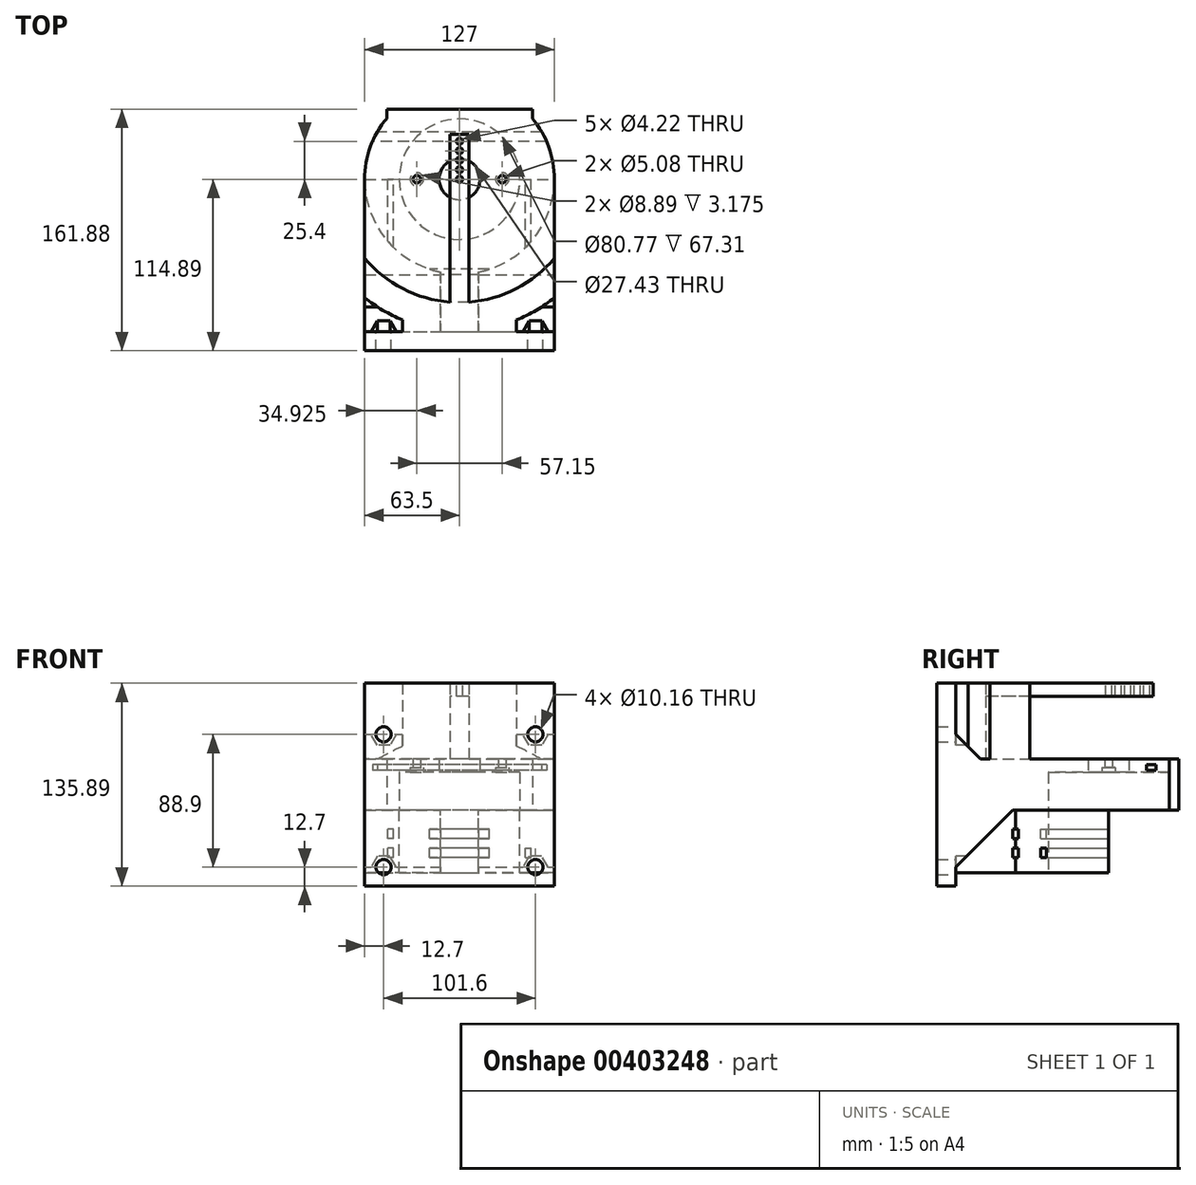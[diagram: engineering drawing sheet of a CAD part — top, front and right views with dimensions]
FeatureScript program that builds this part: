
annotation { "Feature Type Name" : "Feature", "Feature Type Description" : "" }
export const myFeature = defineFeature(function(context is Context, id is Id, definition is map)
    precondition{}
    {
        {
            var Q0;
            Q0=qCreatedBy(makeId("Top.planeOp"),FACE);
            var sketch = newSketch(context, id + "F0", { "sketchPlane" : qUnion([Q0])});
            skCircle(sketch, "E0", {"center": v(0, 0) * mm, "radius": 40.39 * mm});
            skArc(sketch, "E1", {"start": v(63.5, 0) * mm, "mid": v(0, 63.5) * mm, "end": v(-63.5, 0) * mm});
            skLineSegment(sketch, "E2.top", {"start": v(63.5, -102.19) * mm, "end": v(-63.5, -102.19) * mm});
            skLineSegment(sketch, "E2.left", {"start": v(63.5, 0) * mm, "end": v(63.5, -102.19) * mm});
            skLineSegment(sketch, "E2.right", {"start": v(-63.5, 0) * mm, "end": v(-63.5, -102.19) * mm});
            skSolve(sketch);
        }
        {
            var Q0;
            Q0 = qSketchRegion(id + "F0", true);
            extrude(context, id + "F1", {"entities" : qUnion([Q0]), "depth" : 25.4 * mm});
        }
        {
            var Q0;
            Q0=makeQuery(id+"F1.opExtrude","CAP_FACE",FACE,{"disambiguationData":[OSD([sQuery(id+"F0.wireOp",EDGE,"E0"),sQuery(id+"F0.wireOp",EDGE,"E1"),sQuery(id+"F0.wireOp",EDGE,"E2.top"),sQuery(id+"F0.wireOp",EDGE,"E2.left"),sQuery(id+"F0.wireOp",EDGE,"E2.right")])],"isStart":false});
            var sketch = newSketch(context, id + "F2", { "sketchPlane" : qUnion([Q0])});
            skCircle(sketch, "E3", {"center": v(0, 0) * mm, "radius": 63.5 * mm});
            skCircle(sketch, "E4", {"center": v(0, 0) * mm, "radius": 13.72 * mm});
            skLineSegment(sketch, "E5", {"start": v(0, 0) * mm, "end": v(28.58, 0) * mm});
            skLineSegment(sketch, "E6", {"start": v(0, 0) * mm, "end": v(-28.58, 0) * mm});
            skCircle(sketch, "E7", {"center": v(28.58, 0) * mm, "radius": 2.54 * mm});
            skCircle(sketch, "E8", {"center": v(-28.58, 0) * mm, "radius": 2.54 * mm});
            skCircle(sketch, "E9", {"center": v(0, 0) * mm, "radius": 40.4 * mm});
            skSolve(sketch);
        }
        {
            var Q0;
            Q0 = qSketchRegion(id + "F2", true);
            var Q1;
            Q1=makeQuery(id+"F2.imprint","IMPRINT",FACE,{"disambiguationData":[TD([[makeQuery(id+"F2.imprint","IMPRINT",EDGE,{"derivedFrom":sQuery(id+"F2.wireOp",EDGE,"E7")}),-1.0]])]});
            extrude(context, id + "F3", {"entities" : qUnion([Q0, Q1]), "operationType" : NewBodyOperationType.ADD, "depth" : 8.9 * mm});
        }
        {
            var Q0;
            Q0=makeQuery(id+"F1.opExtrude","SWEPT_FACE",FACE,{"disambiguationData":[OSD([sQuery(id+"F0.wireOp",EDGE,"E2.top")])]});
            var sketch = newSketch(context, id + "F4", { "sketchPlane" : qUnion([Q0])});
            skLineSegment(sketch, "E10.bottom", {"start": v(-63.5, 25.4) * mm, "end": v(63.5, 25.4) * mm});
            skLineSegment(sketch, "E10.top", {"start": v(-63.5, 0) * mm, "end": v(63.5, 0) * mm});
            skLineSegment(sketch, "E10.left", {"start": v(-63.5, 25.4) * mm, "end": v(-63.5, 0) * mm});
            skLineSegment(sketch, "E10.right", {"start": v(63.5, 25.4) * mm, "end": v(63.5, 0) * mm});
            skLineSegment(sketch, "E11.top", {"start": v(-63.5, 76.2) * mm, "end": v(63.5, 76.2) * mm});
            skLineSegment(sketch, "E11.left", {"start": v(-63.5, 25.4) * mm, "end": v(-63.5, 76.2) * mm});
            skLineSegment(sketch, "E11.right", {"start": v(63.5, 25.4) * mm, "end": v(63.5, 76.2) * mm});
            skLineSegment(sketch, "E12.top", {"start": v(-63.5, -50.8) * mm, "end": v(63.5, -50.8) * mm});
            skLineSegment(sketch, "E12.left", {"start": v(-63.5, 0) * mm, "end": v(-63.5, -50.8) * mm});
            skLineSegment(sketch, "E12.right", {"start": v(63.5, 0) * mm, "end": v(63.5, -50.8) * mm});
            skSolve(sketch);
        }
        {
            var Q0;
            Q0=makeQuery(id+"F4.imprint","IMPRINT",FACE,{"disambiguationData":[TD([[makeQuery(id+"F4.imprint","IMPRINT",EDGE,{"derivedFrom":sQuery(id+"F4.wireOp",EDGE,"E10.bottom")}),-1.0]])]});
            var Q1;
            Q1=makeQuery(id+"F4.imprint","IMPRINT",FACE,{"disambiguationData":[TD([[makeQuery(id+"F4.imprint","IMPRINT",EDGE,{"derivedFrom":sQuery(id+"F4.wireOp",EDGE,"E10.left")}),1.0]])]});
            var Q2;
            Q2=makeQuery(id+"F4.imprint","IMPRINT",FACE,{"disambiguationData":[TD([[makeQuery(id+"F4.imprint","IMPRINT",EDGE,{"derivedFrom":sQuery(id+"F4.wireOp",EDGE,"E10.top")}),1.0]])]});
            extrude(context, id + "F5", {"entities" : qUnion([Q0, Q1, Q2]), "operationType" : NewBodyOperationType.ADD, "depth" : 12.7 * mm});
        }
        {
            var Q0;
            Q0=makeQuery(id+"F5.boolean.opBoolean","MERGE",FACE,{"derivedFrom":[makeQuery(id+"F1.opExtrude","SWEPT_FACE",FACE,{"disambiguationData":[OSD([sQuery(id+"F0.wireOp",EDGE,"E2.left")])]}),makeQuery(id+"F5.opExtrude","SWEPT_FACE",FACE,{"disambiguationData":[OSD([sQuery(id+"F4.wireOp",EDGE,"E10.right"),sQuery(id+"F4.wireOp",EDGE,"E11.right"),sQuery(id+"F4.wireOp",EDGE,"E12.right")])]})]});
            var sketch = newSketch(context, id + "F6", { "sketchPlane" : qUnion([Q0])});
            skLineSegment(sketch, "E13.bottom", {"start": v(-102.19, 25.4) * mm, "end": v(-76.79, 25.4) * mm});
            skLineSegment(sketch, "E13.top", {"start": v(-102.19, 50.8) * mm, "end": v(-76.79, 50.8) * mm});
            skLineSegment(sketch, "E13.left", {"start": v(-102.19, 25.4) * mm, "end": v(-102.19, 50.8) * mm});
            skLineSegment(sketch, "E13.right", {"start": v(-76.79, 25.4) * mm, "end": v(-76.79, 50.8) * mm});
            skLineSegment(sketch, "E14.bottom", {"start": v(-102.19, 0) * mm, "end": v(-64.09, 0) * mm});
            skLineSegment(sketch, "E14.top", {"start": v(-102.19, -38.1) * mm, "end": v(-64.09, -38.1) * mm});
            skLineSegment(sketch, "E14.left", {"start": v(-102.19, 0) * mm, "end": v(-102.19, -38.1) * mm});
            skLineSegment(sketch, "E14.right", {"start": v(-64.09, 0) * mm, "end": v(-64.09, -38.1) * mm});
            skLineSegment(sketch, "E15", {"start": v(-102.19, -38.1) * mm, "end": v(-64.09, 0) * mm});
            skLineSegment(sketch, "E16", {"start": v(-76.79, 25.4) * mm, "end": v(-102.19, 50.8) * mm});
            skSolve(sketch);
        }
        {
            var Q0;
            Q0=makeQuery(id+"F6.imprint","IMPRINT",FACE,{"disambiguationData":[TD([[makeQuery(id+"F6.imprint","IMPRINT",EDGE,{"derivedFrom":sQuery(id+"F6.wireOp",EDGE,"E13.bottom")}),-1.0]])]});
            var Q1;
            Q1=makeQuery(id+"F6.imprint","IMPRINT",FACE,{"disambiguationData":[TD([[makeQuery(id+"F6.imprint","IMPRINT",EDGE,{"derivedFrom":sQuery(id+"F6.wireOp",EDGE,"E14.bottom")}),1.0]])]});
            extrude(context, id + "F7", {"entities" : qUnion([Q0, Q1]), "operationType" : NewBodyOperationType.ADD, "oppositeDirection" : true, "depth" : 127 * mm});
        }
        {
            var Q0;
            Q0=makeQuery(id+"F3.boolean.opBoolean","MERGE",FACE,{"derivedFrom":[makeQuery(id+"F3.opExtrude","CAP_FACE",FACE,{"disambiguationData":[OSD([sQuery(id+"F2.wireOp",EDGE,"E3"),sQuery(id+"F2.wireOp",EDGE,"E9")])],"isStart":false}),makeQuery(id+"F3.opExtrude","CAP_FACE",FACE,{"disambiguationData":[OSD([sQuery(id+"F0.wireOp",EDGE,"E0"),sQuery(id+"F2.wireOp",EDGE,"E4"),sQuery(id+"F2.wireOp",EDGE,"E7"),sQuery(id+"F2.wireOp",EDGE,"E8")])],"isStart":false})]});
            var sketch = newSketch(context, id + "F8", { "sketchPlane" : qUnion([Q0])});
            skCircle(sketch, "E17", {"center": v(0, 0) * mm, "radius": 101.6 * mm});
            skSolve(sketch);
        }
        {
            var Q0;
            Q0 = qSketchRegion(id + "F8", true);
            extrude(context, id + "F9", {"entities" : qUnion([Q0]), "operationType" : NewBodyOperationType.REMOVE, "depth" : 25.4 * mm});
        }
        {
            var Q0;
            {var subQ0=sQuery(id+"F4.wireOp",EDGE,"E12.left");var subQ1=sQuery(id+"F4.wireOp",EDGE,"E11.left");var subQ2=sQuery(id+"F4.wireOp",EDGE,"E10.left");var subQ5=sQuery(id+"F4.wireOp",EDGE,"E12.right");var subQ6=sQuery(id+"F4.wireOp",EDGE,"E11.right");var subQ7=sQuery(id+"F4.wireOp",EDGE,"E10.right");var subQ8=sQuery(id+"F4.wireOp",EDGE,"E12.top");Q0=makeQuery(id+"F5.boolean.opBoolean","SPLIT",FACE,{"disambiguationData":[TD([makeQuery(id+"F5.opExtrude","SWEPT_FACE",FACE,{"disambiguationData":[OSD([subQ8])]})])],"derivedFrom":makeQuery(id+"F5.opExtrude","CAP_FACE",FACE,{"disambiguationData":[OSD([subQ2,subQ7,sQuery(id+"F4.wireOp",EDGE,"E11.top"),subQ1,subQ6,subQ8,subQ0,subQ5])],"isStart":true})});}
            var sketch = newSketch(context, id + "F10", { "sketchPlane" : qUnion([Q0])});
            skLineSegment(sketch, "E18.bottom", {"start": v(-63.5, -50.8) * mm, "end": v(63.5, -50.8) * mm});
            skLineSegment(sketch, "E18.top", {"start": v(-63.5, 76.2) * mm, "end": v(63.5, 76.2) * mm});
            skLineSegment(sketch, "E18.left", {"start": v(-63.5, -50.8) * mm, "end": v(-63.5, 76.2) * mm});
            skLineSegment(sketch, "E18.right", {"start": v(63.5, -50.8) * mm, "end": v(63.5, 76.2) * mm});
            skLineSegment(sketch, "E19.bottom", {"start": v(-63.5, -50.8) * mm, "end": v(-38.1, -50.8) * mm});
            skLineSegment(sketch, "E19.top", {"start": v(-63.5, -25.4) * mm, "end": v(-38.1, -25.4) * mm});
            skLineSegment(sketch, "E19.left", {"start": v(-63.5, -50.8) * mm, "end": v(-63.5, -25.4) * mm});
            skLineSegment(sketch, "E19.right", {"start": v(-38.1, -50.8) * mm, "end": v(-38.1, -25.4) * mm});
            skLineSegment(sketch, "E20.bottom", {"start": v(63.5, -50.8) * mm, "end": v(38.1, -50.8) * mm});
            skLineSegment(sketch, "E20.top", {"start": v(63.5, -25.4) * mm, "end": v(38.1, -25.4) * mm});
            skLineSegment(sketch, "E20.left", {"start": v(63.5, -50.8) * mm, "end": v(63.5, -25.4) * mm});
            skLineSegment(sketch, "E20.right", {"start": v(38.1, -50.8) * mm, "end": v(38.1, -25.4) * mm});
            skLineSegment(sketch, "E21.bottom", {"start": v(-63.5, 76.2) * mm, "end": v(-50.8, 76.2) * mm});
            skLineSegment(sketch, "E21.top", {"start": v(-63.5, 50.8) * mm, "end": v(-50.8, 50.8) * mm});
            skLineSegment(sketch, "E21.left", {"start": v(-63.5, 76.2) * mm, "end": v(-63.5, 50.8) * mm});
            skLineSegment(sketch, "E21.right", {"start": v(-50.8, 76.2) * mm, "end": v(-50.8, 50.8) * mm});
            skLineSegment(sketch, "E22.bottom", {"start": v(63.5, 76.2) * mm, "end": v(50.8, 76.2) * mm});
            skLineSegment(sketch, "E22.top", {"start": v(63.5, 50.8) * mm, "end": v(50.8, 50.8) * mm});
            skLineSegment(sketch, "E22.left", {"start": v(63.5, 76.2) * mm, "end": v(63.5, 50.8) * mm});
            skLineSegment(sketch, "E22.right", {"start": v(50.8, 76.2) * mm, "end": v(50.8, 50.8) * mm});
            skCircle(sketch, "E23.cCircle", {"center": v(-50.8, 50.8) * mm, "radius": 7.3 * mm, "construction": true});
            skLineSegment(sketch, "E23.0", {"start": v(-46.57, 58.1) * mm, "end": v(-42.37, 50.79) * mm});
            skLineSegment(sketch, "E23.1", {"start": v(-42.37, 50.79) * mm, "end": v(-46.6, 43.5) * mm});
            skLineSegment(sketch, "E23.2", {"start": v(-46.6, 43.5) * mm, "end": v(-55.03, 43.5) * mm});
            skLineSegment(sketch, "E23.3", {"start": v(-55.03, 43.5) * mm, "end": v(-59.23, 50.81) * mm});
            skLineSegment(sketch, "E23.4", {"start": v(-59.23, 50.81) * mm, "end": v(-55, 58.1) * mm});
            skLineSegment(sketch, "E23.5", {"start": v(-55, 58.1) * mm, "end": v(-46.57, 58.1) * mm});
            skPoint(sketch, "E23.0.midPoint", {"position": v(-44.47, 54.44) * mm});
            skLineSegment(sketch, "E24.0.1.0", {"start": v(-46.6, -45.4) * mm, "end": v(-55.03, -45.4) * mm});
            skLineSegment(sketch, "E24.0.1.1", {"start": v(-55.03, -45.4) * mm, "end": v(-59.23, -38.09) * mm});
            skPoint(sketch, "E24.0.1.2", {"position": v(-44.47, -34.46) * mm});
            skLineSegment(sketch, "E24.0.1.3", {"start": v(-42.37, -38.11) * mm, "end": v(-46.6, -45.4) * mm});
            skLineSegment(sketch, "E24.0.1.4", {"start": v(-59.23, -38.09) * mm, "end": v(-55, -30.8) * mm});
            skCircle(sketch, "E24.0.1.5", {"center": v(-50.8, -38.1) * mm, "radius": 7.3 * mm, "construction": true});
            skLineSegment(sketch, "E24.0.1.6", {"start": v(-55, -30.8) * mm, "end": v(-46.57, -30.8) * mm});
            skLineSegment(sketch, "E24.0.1.7", {"start": v(-46.57, -30.8) * mm, "end": v(-42.37, -38.11) * mm});
            skLineSegment(sketch, "E24.1.0.0", {"start": v(55, 43.5) * mm, "end": v(46.57, 43.5) * mm});
            skLineSegment(sketch, "E24.1.0.1", {"start": v(46.57, 43.5) * mm, "end": v(42.37, 50.81) * mm});
            skPoint(sketch, "E24.1.0.2", {"position": v(57.13, 54.44) * mm});
            skLineSegment(sketch, "E24.1.0.3", {"start": v(59.23, 50.79) * mm, "end": v(55, 43.5) * mm});
            skLineSegment(sketch, "E24.1.0.4", {"start": v(42.37, 50.81) * mm, "end": v(46.6, 58.1) * mm});
            skCircle(sketch, "E24.1.0.5", {"center": v(50.8, 50.8) * mm, "radius": 7.3 * mm, "construction": true});
            skLineSegment(sketch, "E24.1.0.6", {"start": v(46.6, 58.1) * mm, "end": v(55.03, 58.1) * mm});
            skLineSegment(sketch, "E24.1.0.7", {"start": v(55.03, 58.1) * mm, "end": v(59.23, 50.79) * mm});
            skLineSegment(sketch, "E24.1.1.0", {"start": v(55, -45.4) * mm, "end": v(46.57, -45.4) * mm});
            skLineSegment(sketch, "E24.1.1.1", {"start": v(46.57, -45.4) * mm, "end": v(42.37, -38.09) * mm});
            skPoint(sketch, "E24.1.1.2", {"position": v(57.13, -34.46) * mm});
            skLineSegment(sketch, "E24.1.1.3", {"start": v(59.23, -38.11) * mm, "end": v(55, -45.4) * mm});
            skLineSegment(sketch, "E24.1.1.4", {"start": v(42.37, -38.09) * mm, "end": v(46.6, -30.8) * mm});
            skCircle(sketch, "E24.1.1.5", {"center": v(50.8, -38.1) * mm, "radius": 7.3 * mm, "construction": true});
            skLineSegment(sketch, "E24.1.1.6", {"start": v(46.6, -30.8) * mm, "end": v(55.03, -30.8) * mm});
            skLineSegment(sketch, "E24.1.1.7", {"start": v(55.03, -30.8) * mm, "end": v(59.23, -38.11) * mm});
            skLineSegment(sketch, "E24.direction1", {"start": v(-55.03, 43.5) * mm, "end": v(46.57, 43.5) * mm, "construction": true});
            skLineSegment(sketch, "E24.direction2", {"start": v(-55.03, 43.5) * mm, "end": v(-55.03, -45.4) * mm, "construction": true});
            skSolve(sketch);
        }
        {
            var Q0;
            {var subQ7=sQuery(id+"F10.wireOp",EDGE,"E23.0");Q0=makeQuery(id+"F10.imprint","IMPRINT",FACE,{"disambiguationData":[TD([[makeQuery(id+"F10.imprint","IMPRINT",EDGE,{"derivedFrom":subQ7}),-1.0]])]});}
            var Q1;
            {var subQ0=sQuery(id+"F10.wireOp",EDGE,"E23.4");Q1=makeQuery(id+"F10.imprint","IMPRINT",FACE,{"disambiguationData":[TD([[makeQuery(id+"F10.imprint","IMPRINT",EDGE,{"derivedFrom":subQ0}),-1.0]])]});}
            var Q2;
            Q2=makeQuery(id+"F10.imprint","IMPRINT",FACE,{"disambiguationData":[TD([[makeQuery(id+"F10.imprint","IMPRINT",EDGE,{"derivedFrom":sQuery(id+"F10.wireOp",EDGE,"E24.1.0.0")}),-1.0]])]});
            var Q3;
            {var subQ0=sQuery(id+"F10.wireOp",EDGE,"E22.right");var subQ1=sQuery(id+"F10.wireOp",EDGE,"E22.top");var subQ2=makeQuery(id+"F10.imprint","INTERSECT",VERTEX,{"derivedFrom":[subQ1,subQ0]});Q3=makeQuery(id+"F10.imprint","IMPRINT",FACE,{"disambiguationData":[TD([[makeQuery(id+"F10.imprint","IMPRINT",EDGE,{"disambiguationData":[TD([[subQ2,1.0]])],"derivedFrom":subQ1}),-1.0]])]});}
            var Q4;
            {var subQ6=sQuery(id+"F10.wireOp",EDGE,"E24.1.1.0");Q4=makeQuery(id+"F10.imprint","IMPRINT",FACE,{"disambiguationData":[TD([[makeQuery(id+"F10.imprint","IMPRINT",EDGE,{"derivedFrom":subQ6}),-1.0]])]});}
            var Q5;
            {var subQ4=sQuery(id+"F10.wireOp",EDGE,"E24.1.1.4");Q5=makeQuery(id+"F10.imprint","IMPRINT",FACE,{"disambiguationData":[TD([[makeQuery(id+"F10.imprint","IMPRINT",EDGE,{"derivedFrom":subQ4}),-1.0]])]});}
            var Q6;
            {var subQ4=sQuery(id+"F10.wireOp",EDGE,"E24.0.1.4");Q6=makeQuery(id+"F10.imprint","IMPRINT",FACE,{"disambiguationData":[TD([[makeQuery(id+"F10.imprint","IMPRINT",EDGE,{"derivedFrom":subQ4}),-1.0]])]});}
            var Q7;
            {var subQ6=sQuery(id+"F10.wireOp",EDGE,"E24.0.1.0");Q7=makeQuery(id+"F10.imprint","IMPRINT",FACE,{"disambiguationData":[TD([[makeQuery(id+"F10.imprint","IMPRINT",EDGE,{"derivedFrom":subQ6}),-1.0]])]});}
            extrude(context, id + "F11", {"entities" : qUnion([Q0, Q1, Q2, Q3, Q4, Q5, Q6, Q7]), "operationType" : NewBodyOperationType.REMOVE, "depth" : 25.4 * mm});
        }
        {
            var Q0;
            {var subQ0=sQuery(id+"F4.wireOp",EDGE,"E12.left");var subQ1=sQuery(id+"F4.wireOp",EDGE,"E11.left");var subQ2=sQuery(id+"F4.wireOp",EDGE,"E10.left");var subQ5=sQuery(id+"F4.wireOp",EDGE,"E12.right");var subQ6=sQuery(id+"F4.wireOp",EDGE,"E11.right");var subQ7=sQuery(id+"F4.wireOp",EDGE,"E10.right");var subQ8=sQuery(id+"F4.wireOp",EDGE,"E11.top");Q0=makeQuery(id+"F11.boolean.opBoolean","MERGE",FACE,{"derivedFrom":[makeQuery(id+"F5.boolean.opBoolean","SPLIT",FACE,{"disambiguationData":[TD([makeQuery(id+"F5.opExtrude","SWEPT_FACE",FACE,{"disambiguationData":[OSD([subQ8])]})])],"derivedFrom":makeQuery(id+"F5.opExtrude","CAP_FACE",FACE,{"disambiguationData":[OSD([subQ2,subQ7,subQ8,subQ1,subQ6,sQuery(id+"F4.wireOp",EDGE,"E12.top"),subQ0,subQ5])],"isStart":true})}),makeQuery(id+"F11.opExtrude","CAP_FACE",FACE,{"disambiguationData":[OSD([sQuery(id+"F10.wireOp",EDGE,"E23.0"),sQuery(id+"F10.wireOp",EDGE,"E23.1"),sQuery(id+"F10.wireOp",EDGE,"E23.2"),sQuery(id+"F10.wireOp",EDGE,"E23.3"),sQuery(id+"F10.wireOp",EDGE,"E23.4"),sQuery(id+"F10.wireOp",EDGE,"E23.5")])],"isStart":true}),makeQuery(id+"F11.opExtrude","CAP_FACE",FACE,{"disambiguationData":[OSD([sQuery(id+"F10.wireOp",EDGE,"E24.1.0.0"),sQuery(id+"F10.wireOp",EDGE,"E24.1.0.1"),sQuery(id+"F10.wireOp",EDGE,"E24.1.0.3"),sQuery(id+"F10.wireOp",EDGE,"E24.1.0.4"),sQuery(id+"F10.wireOp",EDGE,"E24.1.0.6"),sQuery(id+"F10.wireOp",EDGE,"E24.1.0.7")])],"isStart":true})]});}
            var sketch = newSketch(context, id + "F12", { "sketchPlane" : qUnion([Q0])});
            skLineSegment(sketch, "E25.bottom", {"start": v(-63.5, 76.2) * mm, "end": v(63.5, 76.2) * mm});
            skLineSegment(sketch, "E25.top", {"start": v(-63.5, -50.8) * mm, "end": v(63.5, -50.8) * mm});
            skLineSegment(sketch, "E25.left", {"start": v(-63.5, 76.2) * mm, "end": v(-63.5, -50.8) * mm});
            skLineSegment(sketch, "E25.right", {"start": v(63.5, 76.2) * mm, "end": v(63.5, -50.8) * mm});
            skLineSegment(sketch, "E26.bottom", {"start": v(-63.5, 76.2) * mm, "end": v(-50.8, 76.2) * mm});
            skLineSegment(sketch, "E26.top", {"start": v(-63.5, 50.8) * mm, "end": v(-50.8, 50.8) * mm});
            skLineSegment(sketch, "E26.left", {"start": v(-63.5, 76.2) * mm, "end": v(-63.5, 50.8) * mm});
            skLineSegment(sketch, "E26.right", {"start": v(-50.8, 76.2) * mm, "end": v(-50.8, 50.8) * mm});
            skLineSegment(sketch, "E27.bottom", {"start": v(63.5, 76.2) * mm, "end": v(50.8, 76.2) * mm});
            skLineSegment(sketch, "E27.top", {"start": v(63.5, 50.8) * mm, "end": v(50.8, 50.8) * mm});
            skLineSegment(sketch, "E27.left", {"start": v(63.5, 76.2) * mm, "end": v(63.5, 50.8) * mm});
            skLineSegment(sketch, "E27.right", {"start": v(50.8, 76.2) * mm, "end": v(50.8, 50.8) * mm});
            skLineSegment(sketch, "E28.bottom", {"start": v(-63.5, -50.8) * mm, "end": v(-50.8, -50.8) * mm});
            skLineSegment(sketch, "E28.top", {"start": v(-63.5, -38.1) * mm, "end": v(-50.8, -38.1) * mm});
            skLineSegment(sketch, "E28.left", {"start": v(-63.5, -50.8) * mm, "end": v(-63.5, -38.1) * mm});
            skLineSegment(sketch, "E28.right", {"start": v(-50.8, -50.8) * mm, "end": v(-50.8, -38.1) * mm});
            skLineSegment(sketch, "E29.bottom", {"start": v(63.5, -50.8) * mm, "end": v(50.8, -50.8) * mm});
            skLineSegment(sketch, "E29.top", {"start": v(63.5, -38.1) * mm, "end": v(50.8, -38.1) * mm});
            skLineSegment(sketch, "E29.left", {"start": v(63.5, -50.8) * mm, "end": v(63.5, -38.1) * mm});
            skLineSegment(sketch, "E29.right", {"start": v(50.8, -50.8) * mm, "end": v(50.8, -38.1) * mm});
            skCircle(sketch, "E30", {"center": v(-50.8, -38.1) * mm, "radius": 5.08 * mm});
            skCircle(sketch, "E31", {"center": v(50.8, -38.1) * mm, "radius": 5.08 * mm});
            skCircle(sketch, "E32", {"center": v(50.8, 50.8) * mm, "radius": 5.08 * mm});
            skCircle(sketch, "E33", {"center": v(-50.8, 50.8) * mm, "radius": 5.08 * mm});
            skSolve(sketch);
        }
        {
            var Q0;
            {var subQ0=sQuery(id+"F12.wireOp",EDGE,"E26.right");var subQ1=sQuery(id+"F12.wireOp",EDGE,"E26.top");var subQ2=makeQuery(id+"F12.imprint","INTERSECT",VERTEX,{"derivedFrom":[subQ1,subQ0]});Q0=makeQuery(id+"F12.imprint","IMPRINT",FACE,{"disambiguationData":[TD([[makeQuery(id+"F12.imprint","IMPRINT",EDGE,{"disambiguationData":[TD([[subQ2,1.0]])],"derivedFrom":subQ1}),1.0]])]});}
            var Q1;
            {var subQ0=sQuery(id+"F12.wireOp",EDGE,"E26.right");var subQ1=sQuery(id+"F12.wireOp",EDGE,"E26.top");var subQ2=makeQuery(id+"F12.imprint","INTERSECT",VERTEX,{"derivedFrom":[subQ1,subQ0]});Q1=makeQuery(id+"F12.imprint","IMPRINT",FACE,{"disambiguationData":[TD([[makeQuery(id+"F12.imprint","IMPRINT",EDGE,{"disambiguationData":[TD([[subQ2,1.0]])],"derivedFrom":subQ1}),-1.0]])]});}
            var Q2;
            {var subQ0=sQuery(id+"F12.wireOp",EDGE,"E27.right");var subQ1=sQuery(id+"F12.wireOp",EDGE,"E27.top");var subQ2=makeQuery(id+"F12.imprint","INTERSECT",VERTEX,{"derivedFrom":[subQ1,subQ0]});Q2=makeQuery(id+"F12.imprint","IMPRINT",FACE,{"disambiguationData":[TD([[makeQuery(id+"F12.imprint","IMPRINT",EDGE,{"disambiguationData":[TD([[subQ2,1.0]])],"derivedFrom":subQ1}),-1.0]])]});}
            var Q3;
            {var subQ0=sQuery(id+"F12.wireOp",EDGE,"E27.right");var subQ1=sQuery(id+"F12.wireOp",EDGE,"E27.top");var subQ2=makeQuery(id+"F12.imprint","INTERSECT",VERTEX,{"derivedFrom":[subQ1,subQ0]});Q3=makeQuery(id+"F12.imprint","IMPRINT",FACE,{"disambiguationData":[TD([[makeQuery(id+"F12.imprint","IMPRINT",EDGE,{"disambiguationData":[TD([[subQ2,1.0]])],"derivedFrom":subQ1}),1.0]])]});}
            var Q4;
            {var subQ0=sQuery(id+"F12.wireOp",EDGE,"E29.right");var subQ1=sQuery(id+"F12.wireOp",EDGE,"E29.top");var subQ2=makeQuery(id+"F12.imprint","INTERSECT",VERTEX,{"derivedFrom":[subQ1,subQ0]});Q4=makeQuery(id+"F12.imprint","IMPRINT",FACE,{"disambiguationData":[TD([[makeQuery(id+"F12.imprint","IMPRINT",EDGE,{"disambiguationData":[TD([[subQ2,1.0]])],"derivedFrom":subQ1}),1.0]])]});}
            var Q5;
            {var subQ0=sQuery(id+"F12.wireOp",EDGE,"E29.right");var subQ1=sQuery(id+"F12.wireOp",EDGE,"E29.top");var subQ2=makeQuery(id+"F12.imprint","INTERSECT",VERTEX,{"derivedFrom":[subQ1,subQ0]});Q5=makeQuery(id+"F12.imprint","IMPRINT",FACE,{"disambiguationData":[TD([[makeQuery(id+"F12.imprint","IMPRINT",EDGE,{"disambiguationData":[TD([[subQ2,1.0]])],"derivedFrom":subQ1}),-1.0]])]});}
            var Q6;
            {var subQ0=sQuery(id+"F12.wireOp",EDGE,"E28.right");var subQ1=sQuery(id+"F12.wireOp",EDGE,"E28.top");var subQ2=makeQuery(id+"F12.imprint","INTERSECT",VERTEX,{"derivedFrom":[subQ1,subQ0]});Q6=makeQuery(id+"F12.imprint","IMPRINT",FACE,{"disambiguationData":[TD([[makeQuery(id+"F12.imprint","IMPRINT",EDGE,{"disambiguationData":[TD([[subQ2,1.0]])],"derivedFrom":subQ1}),1.0]])]});}
            var Q7;
            {var subQ0=sQuery(id+"F12.wireOp",EDGE,"E28.right");var subQ1=sQuery(id+"F12.wireOp",EDGE,"E28.top");var subQ2=makeQuery(id+"F12.imprint","INTERSECT",VERTEX,{"derivedFrom":[subQ1,subQ0]});Q7=makeQuery(id+"F12.imprint","IMPRINT",FACE,{"disambiguationData":[TD([[makeQuery(id+"F12.imprint","IMPRINT",EDGE,{"disambiguationData":[TD([[subQ2,1.0]])],"derivedFrom":subQ1}),-1.0]])]});}
            extrude(context, id + "F13", {"entities" : qUnion([Q0, Q1, Q2, Q3, Q4, Q5, Q6, Q7]), "operationType" : NewBodyOperationType.REMOVE, "oppositeDirection" : true, "depth" : 25.4 * mm});
        }
        {
            var Q0;
            Q0=makeQuery(id+"F1.opExtrude","CAP_FACE",FACE,{"disambiguationData":[OSD([sQuery(id+"F0.wireOp",EDGE,"E0"),sQuery(id+"F0.wireOp",EDGE,"E1"),sQuery(id+"F0.wireOp",EDGE,"E2.top"),sQuery(id+"F0.wireOp",EDGE,"E2.left"),sQuery(id+"F0.wireOp",EDGE,"E2.right")])],"isStart":false});
            var sketch = newSketch(context, id + "F14", { "sketchPlane" : qUnion([Q0])});
            skLineSegment(sketch, "E34.bottom", {"start": v(63.5, 0) * mm, "end": v(44.72, 0) * mm});
            skLineSegment(sketch, "E34.top", {"start": v(63.5, -88.9) * mm, "end": v(-63.5, -88.9) * mm});
            skLineSegment(sketch, "E34.left", {"start": v(63.5, 0) * mm, "end": v(63.5, -88.9) * mm});
            skLineSegment(sketch, "E34.right", {"start": v(-63.5, 0) * mm, "end": v(-63.5, -88.9) * mm});
            skLineSegment(sketch, "E35.top", {"start": v(44.72, -22.33) * mm, "end": v(-44.71, -22.33) * mm});
            skLineSegment(sketch, "E35.left", {"start": v(44.72, 0) * mm, "end": v(44.72, -22.33) * mm});
            skLineSegment(sketch, "E35.right", {"start": v(-44.71, 0) * mm, "end": v(-44.71, -22.33) * mm});
            skLineSegment(sketch, "E36.trimOffspring", {"start": v(-44.71, 0) * mm, "end": v(-63.5, 0) * mm});
            skSolve(sketch);
        }
        {
            var Q0;
            Q0 = qSketchRegion(id + "F14", true);
            extrude(context, id + "F15", {"entities" : qUnion([Q0]), "operationType" : NewBodyOperationType.ADD, "depth" : 8.9 * mm});
        }
        {
            var Q0;
            Q0=makeQuery(id+"F3.boolean.opBoolean","MERGE",FACE,{"derivedFrom":[makeQuery(id+"F3.opExtrude","CAP_FACE",FACE,{"disambiguationData":[OSD([sQuery(id+"F2.wireOp",EDGE,"E3"),sQuery(id+"F2.wireOp",EDGE,"E9")])],"isStart":true}),makeQuery(id+"F3.opExtrude","CAP_FACE",FACE,{"disambiguationData":[OSD([sQuery(id+"F0.wireOp",EDGE,"E0"),sQuery(id+"F2.wireOp",EDGE,"E4"),sQuery(id+"F2.wireOp",EDGE,"E7"),sQuery(id+"F2.wireOp",EDGE,"E8")])],"isStart":true})]});
            var sketch = newSketch(context, id + "F16", { "sketchPlane" : qUnion([Q0])});
            skCircle(sketch, "E37", {"center": v(-28.58, 0) * mm, "radius": 4.45 * mm});
            skCircle(sketch, "E38", {"center": v(28.58, 0) * mm, "radius": 4.45 * mm});
            skSolve(sketch);
        }
        {
            var Q0;
            Q0 = qSketchRegion(id + "F16", true);
            extrude(context, id + "F17", {"entities" : qUnion([Q0]), "operationType" : NewBodyOperationType.REMOVE, "oppositeDirection" : true, "depth" : 3.17 * mm});
        }
        {
            var Q0;
            Q0=makeQuery(id+"F15.boolean.opBoolean","MERGE",FACE,{"derivedFrom":[makeQuery(id+"F3.boolean.opBoolean","MERGE",FACE,{"derivedFrom":[makeQuery(id+"F3.opExtrude","CAP_FACE",FACE,{"disambiguationData":[OSD([sQuery(id+"F2.wireOp",EDGE,"E3"),sQuery(id+"F2.wireOp",EDGE,"E9")])],"isStart":false}),makeQuery(id+"F3.opExtrude","CAP_FACE",FACE,{"disambiguationData":[OSD([sQuery(id+"F0.wireOp",EDGE,"E0"),sQuery(id+"F2.wireOp",EDGE,"E4"),sQuery(id+"F2.wireOp",EDGE,"E7"),sQuery(id+"F2.wireOp",EDGE,"E8")])],"isStart":false})]}),makeQuery(id+"F9.boolean.opBoolean","COPY",FACE,{"derivedFrom":makeQuery(id+"F9.opExtrude","CAP_FACE",FACE,{"disambiguationData":[OSD([sQuery(id+"F8.wireOp",EDGE,"E17")])],"isStart":true})}),makeQuery(id+"F15.opExtrude","CAP_FACE",FACE,{"disambiguationData":[OSD([sQuery(id+"F14.wireOp",EDGE,"E34.bottom"),sQuery(id+"F14.wireOp",EDGE,"E34.top"),sQuery(id+"F14.wireOp",EDGE,"E34.left"),sQuery(id+"F14.wireOp",EDGE,"E34.right"),sQuery(id+"F14.wireOp",EDGE,"E35.top"),sQuery(id+"F14.wireOp",EDGE,"E35.left"),sQuery(id+"F14.wireOp",EDGE,"E35.right"),sQuery(id+"F14.wireOp",EDGE,"E36.trimOffspring")])],"isStart":false})]});
            var sketch = newSketch(context, id + "F18", { "sketchPlane" : qUnion([Q0])});
            skArc(sketch, "E39", {"start": v(-63.5, -79.31) * mm, "mid": v(0, -101.6) * mm, "end": v(63.5, -79.31) * mm});
            skArc(sketch, "E40", {"start": v(-63.5, -71) * mm, "mid": v(0, -95.25) * mm, "end": v(63.5, -71) * mm});
            skLineSegment(sketch, "E41", {"start": v(63.5, -79.31) * mm, "end": v(63.5, -71) * mm});
            skLineSegment(sketch, "E42", {"start": v(-63.5, -79.31) * mm, "end": v(-63.5, -71) * mm});
            skSolve(sketch);
        }
        {
            var Q0;
            Q0 = qSketchRegion(id + "F18", true);
            extrude(context, id + "F19", {"entities" : qUnion([Q0]), "operationType" : NewBodyOperationType.ADD, "depth" : 50.8 * mm});
        }
        {
            var Q0;
            Q0=makeQuery(id+"F1.opExtrude","CAP_FACE",FACE,{"disambiguationData":[OSD([sQuery(id+"F0.wireOp",EDGE,"E0"),sQuery(id+"F0.wireOp",EDGE,"E1"),sQuery(id+"F0.wireOp",EDGE,"E2.top"),sQuery(id+"F0.wireOp",EDGE,"E2.left"),sQuery(id+"F0.wireOp",EDGE,"E2.right")])],"isStart":true});
            var sketch = newSketch(context, id + "F20", { "sketchPlane" : qUnion([Q0])});
            skCircle(sketch, "E43", {"center": v(0, 0) * mm, "radius": 40.39 * mm});
            skCircle(sketch, "E44", {"center": v(0, 0) * mm, "radius": 63.5 * mm});
            skLineSegment(sketch, "E45", {"start": v(0, 0) * mm, "end": v(12.7, 0) * mm});
            skLineSegment(sketch, "E46.bottom", {"start": v(12.7, 0) * mm, "end": v(-12.7, 0) * mm});
            skLineSegment(sketch, "E46.top", {"start": v(12.7, 114.3) * mm, "end": v(-12.7, 114.3) * mm});
            skLineSegment(sketch, "E46.left", {"start": v(12.7, 0) * mm, "end": v(12.7, 114.3) * mm});
            skLineSegment(sketch, "E46.right", {"start": v(-12.7, 0) * mm, "end": v(-12.7, 114.3) * mm});
            skLineSegment(sketch, "E47", {"start": v(-63.5, 0) * mm, "end": v(63.5, 0) * mm});
            skSolve(sketch);
        }
        {
            var Q0;
            {var subQ0=sQuery(id+"F20.wireOp",EDGE,"E47");var subQ1=sQuery(id+"F20.wireOp",EDGE,"E43");var subQ2=makeQuery(id+"F20.imprint","INTERSECT",VERTEX,{"disambiguationData":[OD(0.0)],"derivedFrom":[subQ1,subQ0]});Q0=makeQuery(id+"F20.imprint","IMPRINT",FACE,{"disambiguationData":[TD([[makeQuery(id+"F20.imprint","IMPRINT",EDGE,{"disambiguationData":[TD([[subQ2,-1.0]])],"derivedFrom":subQ1}),1.0]])]});}
            var Q1;
            {var subQ0=sQuery(id+"F20.wireOp",EDGE,"E46.right");var subQ1=sQuery(id+"F20.wireOp",EDGE,"E43");var subQ2=makeQuery(id+"F20.imprint","INTERSECT",VERTEX,{"derivedFrom":[subQ1,subQ0]});Q1=makeQuery(id+"F20.imprint","IMPRINT",FACE,{"disambiguationData":[TD([[makeQuery(id+"F20.imprint","IMPRINT",EDGE,{"disambiguationData":[TD([[subQ2,-1.0]])],"derivedFrom":subQ1}),1.0]])]});}
            var Q2;
            {var subQ0=sQuery(id+"F20.wireOp",EDGE,"E47");var subQ1=sQuery(id+"F20.wireOp",EDGE,"E43");var subQ2=makeQuery(id+"F20.imprint","INTERSECT",VERTEX,{"disambiguationData":[OD(1.0)],"derivedFrom":[subQ1,subQ0]});Q2=makeQuery(id+"F20.imprint","IMPRINT",FACE,{"disambiguationData":[TD([[makeQuery(id+"F20.imprint","IMPRINT",EDGE,{"disambiguationData":[TD([[subQ2,1.0]])],"derivedFrom":subQ1}),1.0]])]});}
            var Q3;
            {var subQ0=sQuery(id+"F20.wireOp",EDGE,"E46.top");Q3=makeQuery(id+"F20.imprint","IMPRINT",FACE,{"disambiguationData":[TD([[makeQuery(id+"F20.imprint","IMPRINT",EDGE,{"derivedFrom":subQ0}),1.0]])]});}
            var Q4;
            {var subQ0=sQuery(id+"F20.wireOp",EDGE,"E46.left");var subQ1=sQuery(id+"F20.wireOp",EDGE,"E44");var subQ2=makeQuery(id+"F20.imprint","INTERSECT",VERTEX,{"derivedFrom":[subQ1,subQ0]});var subQ3=sQuery(id+"F20.wireOp",EDGE,"E46.right");var subQ4=makeQuery(id+"F20.imprint","INTERSECT",VERTEX,{"derivedFrom":[subQ1,subQ3]});Q4=makeQuery(id+"F20.imprint","IMPRINT",FACE,{"disambiguationData":[TD([[makeQuery(id+"F20.imprint","IMPRINT",EDGE,{"disambiguationData":[TD([[subQ2,-1.0],[subQ4,1.0]])],"derivedFrom":subQ1}),-1.0]])]});}
            extrude(context, id + "F21", {"entities" : qUnion([Q0, Q1, Q2, Q3, Q4]), "operationType" : NewBodyOperationType.ADD, "depth" : 41.9 * mm});
        }
        {
            var Q0;
            Q0=makeQuery(id+"F21.opExtrude","SWEPT_FACE",FACE,{"disambiguationData":[OSD([sQuery(id+"F20.wireOp",EDGE,"E46.right")])]});
            var sketch = newSketch(context, id + "F22", { "sketchPlane" : qUnion([Q0])});
            skLineSegment(sketch, "E48", {"start": v(64.09, 0) * mm, "end": v(64.09, -12.7) * mm});
            skLineSegment(sketch, "E49.bottom", {"start": v(64.09, -12.7) * mm, "end": v(60.28, -12.7) * mm});
            skLineSegment(sketch, "E49.top", {"start": v(64.09, -19.05) * mm, "end": v(60.28, -19.05) * mm});
            skLineSegment(sketch, "E49.left", {"start": v(64.09, -12.7) * mm, "end": v(64.09, -19.05) * mm});
            skLineSegment(sketch, "E49.right", {"start": v(60.28, -12.7) * mm, "end": v(60.28, -19.05) * mm});
            skLineSegment(sketch, "E50", {"start": v(64.09, -19.05) * mm, "end": v(64.09, -25.4) * mm});
            skLineSegment(sketch, "E51.bottom", {"start": v(64.09, -25.4) * mm, "end": v(60.28, -25.4) * mm});
            skLineSegment(sketch, "E51.top", {"start": v(64.09, -31.75) * mm, "end": v(60.28, -31.75) * mm});
            skLineSegment(sketch, "E51.left", {"start": v(64.09, -25.4) * mm, "end": v(64.09, -31.75) * mm});
            skLineSegment(sketch, "E51.right", {"start": v(60.28, -25.4) * mm, "end": v(60.28, -31.75) * mm});
            skSolve(sketch);
        }
        {
            var Q0;
            Q0 = qSketchRegion(id + "F22", true);
            extrude(context, id + "F23", {"entities" : qUnion([Q0]), "operationType" : NewBodyOperationType.REMOVE, "endBound" : BoundingType.SYMMETRIC, "oppositeDirection" : true, "depth" : 76.2 * mm});
        }
        {
            var Q0;
            {var subQ0=sQuery(id+"F20.wireOp",EDGE,"E47");Q0=makeQuery(id+"F21.opExtrude","SWEPT_FACE",FACE,{"disambiguationData":[OSD([subQ0]),TDD([makeQuery(id+"F20.imprint","IMPRINT",EDGE,{"disambiguationData":[TD([[makeQuery(id+"F20.imprint","INTERSECT",VERTEX,{"disambiguationData":[OD(0.0)],"derivedFrom":[sQuery(id+"F20.wireOp",EDGE,"E43"),subQ0]}),1.0]])],"derivedFrom":subQ0})])]});}
            var sketch = newSketch(context, id + "F24", { "sketchPlane" : qUnion([Q0])});
            skLineSegment(sketch, "E52", {"start": v(40.39, 0) * mm, "end": v(40.39, -12.7) * mm});
            skLineSegment(sketch, "E53.bottom", {"start": v(40.39, -12.7) * mm, "end": v(44.2, -12.7) * mm});
            skLineSegment(sketch, "E53.top", {"start": v(40.39, -19.05) * mm, "end": v(44.2, -19.05) * mm});
            skLineSegment(sketch, "E53.left", {"start": v(40.39, -12.7) * mm, "end": v(40.39, -19.05) * mm});
            skLineSegment(sketch, "E53.right", {"start": v(44.2, -12.7) * mm, "end": v(44.2, -19.05) * mm});
            skLineSegment(sketch, "E54", {"start": v(40.39, -19.05) * mm, "end": v(40.39, -25.4) * mm});
            skLineSegment(sketch, "E55.bottom", {"start": v(40.39, -25.4) * mm, "end": v(44.2, -25.4) * mm});
            skLineSegment(sketch, "E55.top", {"start": v(40.39, -31.75) * mm, "end": v(44.2, -31.75) * mm});
            skLineSegment(sketch, "E55.left", {"start": v(40.39, -25.4) * mm, "end": v(40.39, -31.75) * mm});
            skLineSegment(sketch, "E55.right", {"start": v(44.2, -25.4) * mm, "end": v(44.2, -31.75) * mm});
            skLineSegment(sketch, "E56.bottom", {"start": v(44.2, -31.75) * mm, "end": v(48, -31.75) * mm});
            skLineSegment(sketch, "E56.top", {"start": v(44.2, -25.4) * mm, "end": v(48, -25.4) * mm});
            skLineSegment(sketch, "E56.left", {"start": v(44.2, -31.75) * mm, "end": v(44.2, -25.4) * mm});
            skLineSegment(sketch, "E56.right", {"start": v(48, -31.75) * mm, "end": v(48, -25.4) * mm});
            skPoint(sketch, "E57.oppositeSnap0", {"position": v(48, -28.57) * mm});
            skLineSegment(sketch, "E57.bottom", {"start": v(44.2, -19.05) * mm, "end": v(48, -19.05) * mm});
            skLineSegment(sketch, "E57.top", {"start": v(44.2, -12.7) * mm, "end": v(48, -12.7) * mm});
            skLineSegment(sketch, "E57.left", {"start": v(44.2, -19.05) * mm, "end": v(44.2, -12.7) * mm});
            skLineSegment(sketch, "E57.right", {"start": v(48, -19.05) * mm, "end": v(48, -12.7) * mm});
            skLineSegment(sketch, "E58", {"start": v(0, 0) * mm, "end": v(0, -36.16) * mm});
            skLineSegment(sketch, "E59.MirrorCS", {"start": v(-44.2, -25.4) * mm, "end": v(-44.2, -31.75) * mm});
            skLineSegment(sketch, "E60.MirrorCS", {"start": v(-44.2, -19.05) * mm, "end": v(-44.2, -12.7) * mm});
            skLineSegment(sketch, "E61.MirrorCS", {"start": v(-44.2, -12.7) * mm, "end": v(-44.2, -19.05) * mm});
            skLineSegment(sketch, "E62.MirrorCS", {"start": v(-48, -19.05) * mm, "end": v(-48, -12.7) * mm});
            skLineSegment(sketch, "E63.MirrorCS", {"start": v(-44.2, -31.75) * mm, "end": v(-48, -31.75) * mm});
            skLineSegment(sketch, "E64.MirrorCS", {"start": v(-44.2, -12.7) * mm, "end": v(-48, -12.7) * mm});
            skLineSegment(sketch, "E65.MirrorCS", {"start": v(-44.2, -19.05) * mm, "end": v(-48, -19.05) * mm});
            skLineSegment(sketch, "E66.MirrorCS", {"start": v(-48, -31.75) * mm, "end": v(-48, -25.4) * mm});
            skLineSegment(sketch, "E67.MirrorCS", {"start": v(-44.2, -31.75) * mm, "end": v(-44.2, -25.4) * mm});
            skLineSegment(sketch, "E68.MirrorCS", {"start": v(-44.2, -25.4) * mm, "end": v(-48, -25.4) * mm});
            skPoint(sketch, "E69.MirrorP", {"position": v(-48, -28.57) * mm});
            skSolve(sketch);
        }
        {
            var Q0;
            Q0=makeQuery(id+"F24.imprint","IMPRINT",FACE,{"disambiguationData":[TD([[makeQuery(id+"F24.imprint","IMPRINT",EDGE,{"derivedFrom":sQuery(id+"F24.wireOp",EDGE,"E61.MirrorCS")}),-1.0]])]});
            var Q1;
            Q1=makeQuery(id+"F24.imprint","IMPRINT",FACE,{"disambiguationData":[TD([[makeQuery(id+"F24.imprint","IMPRINT",EDGE,{"derivedFrom":sQuery(id+"F24.wireOp",EDGE,"E63.MirrorCS")}),-1.0]])]});
            var Q2;
            Q2=makeQuery(id+"F24.imprint","IMPRINT",FACE,{"disambiguationData":[TD([[makeQuery(id+"F24.imprint","IMPRINT",EDGE,{"derivedFrom":sQuery(id+"F24.wireOp",EDGE,"E56.bottom")}),1.0]])]});
            var Q3;
            Q3=makeQuery(id+"F24.imprint","IMPRINT",FACE,{"disambiguationData":[TD([[makeQuery(id+"F24.imprint","IMPRINT",EDGE,{"derivedFrom":sQuery(id+"F24.wireOp",EDGE,"E57.bottom")}),1.0]])]});
            extrude(context, id + "F25", {"entities" : qUnion([Q0, Q1, Q2, Q3]), "operationType" : NewBodyOperationType.REMOVE, "oppositeDirection" : true, "depth" : 50.8 * mm});
        }
        {
            var Q0;
            Q0=makeQuery(id+"F19.boolean.opBoolean","MERGE",FACE,{"derivedFrom":[makeQuery(id+"F15.boolean.opBoolean","MERGE",FACE,{"derivedFrom":[makeQuery(id+"F7.boolean.opBoolean","MERGE",FACE,{"derivedFrom":[makeQuery(id+"F5.boolean.opBoolean","MERGE",FACE,{"derivedFrom":[makeQuery(id+"F1.opExtrude","SWEPT_FACE",FACE,{"disambiguationData":[OSD([sQuery(id+"F0.wireOp",EDGE,"E2.right")])]}),makeQuery(id+"F5.opExtrude","SWEPT_FACE",FACE,{"disambiguationData":[OSD([sQuery(id+"F4.wireOp",EDGE,"E10.left"),sQuery(id+"F4.wireOp",EDGE,"E11.left"),sQuery(id+"F4.wireOp",EDGE,"E12.left")])]})]}),makeQuery(id+"F7.opExtrude","CAP_FACE",FACE,{"disambiguationData":[OSD([sQuery(id+"F6.wireOp",EDGE,"E13.bottom"),sQuery(id+"F6.wireOp",EDGE,"E13.left"),sQuery(id+"F6.wireOp",EDGE,"E16")])],"isStart":false}),makeQuery(id+"F7.opExtrude","CAP_FACE",FACE,{"disambiguationData":[OSD([sQuery(id+"F6.wireOp",EDGE,"E14.bottom"),sQuery(id+"F6.wireOp",EDGE,"E14.left"),sQuery(id+"F6.wireOp",EDGE,"E15")])],"isStart":false})]}),makeQuery(id+"F15.opExtrude","SWEPT_FACE",FACE,{"disambiguationData":[OSD([sQuery(id+"F14.wireOp",EDGE,"E34.right")])]})]}),makeQuery(id+"F19.opExtrude","SWEPT_FACE",FACE,{"disambiguationData":[OSD([sQuery(id+"F18.wireOp",EDGE,"E42")])]})]});
            var sketch = newSketch(context, id + "F26", { "sketchPlane" : qUnion([Q0])});
            skLineSegment(sketch, "E70.bottom", {"start": v(0, 34.3) * mm, "end": v(-25.4, 34.3) * mm});
            skLineSegment(sketch, "E70.top", {"start": v(0, 30.48) * mm, "end": v(-25.4, 30.48) * mm});
            skLineSegment(sketch, "E70.left", {"start": v(0, 34.3) * mm, "end": v(0, 30.48) * mm});
            skLineSegment(sketch, "E70.right", {"start": v(-25.4, 34.3) * mm, "end": v(-25.4, 30.48) * mm});
            skLineSegment(sketch, "E71.bottom", {"start": v(-25.4, 30.48) * mm, "end": v(-31.75, 30.48) * mm});
            skLineSegment(sketch, "E71.top", {"start": v(-25.4, 26.67) * mm, "end": v(-31.75, 26.67) * mm});
            skLineSegment(sketch, "E71.left", {"start": v(-25.4, 30.48) * mm, "end": v(-25.4, 26.67) * mm});
            skLineSegment(sketch, "E71.right", {"start": v(-31.75, 30.48) * mm, "end": v(-31.75, 26.67) * mm});
            skSolve(sketch);
        }
        {
            var Q0;
            Q0=makeQuery(id+"F26.imprint","IMPRINT",FACE,{"disambiguationData":[TD([[makeQuery(id+"F26.imprint","IMPRINT",EDGE,{"derivedFrom":sQuery(id+"F26.wireOp",EDGE,"E71.bottom")}),1.0]])]});
            extrude(context, id + "F27", {"entities" : qUnion([Q0]), "operationType" : NewBodyOperationType.REMOVE, "endBound" : BoundingType.THROUGH_ALL, "oppositeDirection" : true, "depth" : 25.4 * mm});
        }
        {
            var Q0;
            {var subQ0=sQuery(id+"F20.wireOp",EDGE,"E47");Q0=makeQuery(id+"F21.opExtrude","SWEPT_FACE",FACE,{"disambiguationData":[OSD([subQ0]),TDD([makeQuery(id+"F20.imprint","IMPRINT",EDGE,{"disambiguationData":[TD([[makeQuery(id+"F20.imprint","INTERSECT",VERTEX,{"disambiguationData":[OD(1.0)],"derivedFrom":[sQuery(id+"F20.wireOp",EDGE,"E43"),subQ0]}),-1.0]])],"derivedFrom":subQ0})])]});}
            cPlane(context, id + "F28", {"entities" : qUnion([Q0]), "cplaneType" : CPlaneType.OFFSET, "offset" : 40.64 * mm, "width" : 152.4 * mm, "height" : 152.4 * mm});
        }
        {
            var Q0;
            Q0=qCreatedBy(id+"F28.planeOp",FACE);
            var sketch = newSketch(context, id + "F29", { "sketchPlane" : qUnion([Q0])});
            skLineSegment(sketch, "E72.bottom", {"start": v(112.57, 54.79) * mm, "end": v(-136.53, 54.79) * mm});
            skLineSegment(sketch, "E72.top", {"start": v(112.57, -28.85) * mm, "end": v(-136.53, -28.85) * mm});
            skLineSegment(sketch, "E72.left", {"start": v(112.57, 54.79) * mm, "end": v(112.57, -28.85) * mm});
            skLineSegment(sketch, "E72.right", {"start": v(-136.53, 54.79) * mm, "end": v(-136.53, -28.85) * mm});
            skSolve(sketch);
        }
        {
            var Q0;
            Q0=makeQuery(id+"F29.imprint","IMPRINT",FACE,{"disambiguationData":[TD([[makeQuery(id+"F29.imprint","IMPRINT",EDGE,{"derivedFrom":sQuery(id+"F29.wireOp",EDGE,"E72.bottom")}),1.0]])]});
            extrude(context, id + "F30", {"entities" : qUnion([Q0]), "operationType" : NewBodyOperationType.REMOVE, "depth" : 25.4 * mm});
        }
        {
            var Q0;
            {var subQ0=sQuery(id+"F4.wireOp",EDGE,"E12.left");var subQ1=sQuery(id+"F4.wireOp",EDGE,"E11.left");var subQ2=sQuery(id+"F4.wireOp",EDGE,"E10.left");var subQ5=sQuery(id+"F4.wireOp",EDGE,"E12.right");var subQ6=sQuery(id+"F4.wireOp",EDGE,"E11.right");var subQ7=sQuery(id+"F4.wireOp",EDGE,"E10.right");var subQ8=sQuery(id+"F4.wireOp",EDGE,"E11.top");Q0=makeQuery(id+"F11.boolean.opBoolean","MERGE",FACE,{"derivedFrom":[makeQuery(id+"F5.boolean.opBoolean","SPLIT",FACE,{"disambiguationData":[TD([makeQuery(id+"F5.opExtrude","SWEPT_FACE",FACE,{"disambiguationData":[OSD([subQ8])]})])],"derivedFrom":makeQuery(id+"F5.opExtrude","CAP_FACE",FACE,{"disambiguationData":[OSD([subQ2,subQ7,subQ8,subQ1,subQ6,sQuery(id+"F4.wireOp",EDGE,"E12.top"),subQ0,subQ5])],"isStart":true})}),makeQuery(id+"F11.opExtrude","CAP_FACE",FACE,{"disambiguationData":[OSD([sQuery(id+"F10.wireOp",EDGE,"E23.0"),sQuery(id+"F10.wireOp",EDGE,"E23.1"),sQuery(id+"F10.wireOp",EDGE,"E23.2"),sQuery(id+"F10.wireOp",EDGE,"E23.3"),sQuery(id+"F10.wireOp",EDGE,"E23.4"),sQuery(id+"F10.wireOp",EDGE,"E23.5")])],"isStart":true}),makeQuery(id+"F11.opExtrude","CAP_FACE",FACE,{"disambiguationData":[OSD([sQuery(id+"F10.wireOp",EDGE,"E24.1.0.0"),sQuery(id+"F10.wireOp",EDGE,"E24.1.0.1"),sQuery(id+"F10.wireOp",EDGE,"E24.1.0.3"),sQuery(id+"F10.wireOp",EDGE,"E24.1.0.4"),sQuery(id+"F10.wireOp",EDGE,"E24.1.0.6"),sQuery(id+"F10.wireOp",EDGE,"E24.1.0.7")])],"isStart":true})]});}
            cPlane(context, id + "F31", {"entities" : qUnion([Q0]), "cplaneType" : CPlaneType.OFFSET, "offset" : 5.08 * mm, "width" : 152.4 * mm, "height" : 152.4 * mm});
        }
        {
            var Q0;
            Q0=qCreatedBy(id+"F31.planeOp",FACE);
            var sketch = newSketch(context, id + "F32", { "sketchPlane" : qUnion([Q0])});
            skLineSegment(sketch, "E73", {"start": v(0, 0) * mm, "end": v(0, 82.55) * mm});
            skLineSegment(sketch, "E74.bottom", {"start": v(0, 82.55) * mm, "end": v(6.35, 82.55) * mm});
            skLineSegment(sketch, "E74.top", {"start": v(0, 76.2) * mm, "end": v(6.35, 76.2) * mm});
            skLineSegment(sketch, "E74.left", {"start": v(0, 82.55) * mm, "end": v(0, 76.2) * mm});
            skLineSegment(sketch, "E74.right", {"start": v(6.35, 82.55) * mm, "end": v(6.35, 76.2) * mm});
            skLineSegment(sketch, "E75.bottom", {"start": v(0, 82.55) * mm, "end": v(-6.35, 82.55) * mm});
            skLineSegment(sketch, "E75.top", {"start": v(0, 76.2) * mm, "end": v(-6.35, 76.2) * mm});
            skLineSegment(sketch, "E75.right", {"start": v(-6.35, 82.55) * mm, "end": v(-6.35, 76.2) * mm});
            skSolve(sketch);
        }
        {
            var Q0;
            Q0 = qSketchRegion(id + "F32", true);
            extrude(context, id + "F33", {"entities" : qUnion([Q0]), "operationType" : NewBodyOperationType.ADD, "depth" : 127 * mm});
        }
        {
            var Q0;
            Q0=makeQuery(id+"F33.opExtrude","SWEPT_FACE",FACE,{"disambiguationData":[OSD([sQuery(id+"F32.wireOp",EDGE,"E74.bottom"),sQuery(id+"F32.wireOp",EDGE,"E75.bottom")])]});
            var sketch = newSketch(context, id + "F34", { "sketchPlane" : qUnion([Q0])});
            skSolve(sketch);
        }
        {
            var Q0;
            Q0 = qSketchRegion(id + "F34", true);
            var Q1;
            {var subQ0=sQuery(id+"F32.wireOp",EDGE,"E75.bottom");var subQ1=sQuery(id+"F32.wireOp",EDGE,"E74.bottom");Q1=makeQuery(id+"F34.imprint","IMPRINT",FACE,{"disambiguationData":[TD([[makeQuery(id+"F34.imprint","IMPRINT",EDGE,{"derivedFrom":makeQuery(id+"F33.opExtrude","CAP_EDGE",EDGE,{"disambiguationData":[OSD([subQ1,subQ0])],"isStart":false})}),1.0]])]});}
            extrude(context, id + "F35", {"entities" : qUnion([Q0, Q1]), "operationType" : NewBodyOperationType.ADD, "depth" : 2.54 * mm});
        }
        {
            var Q0;
            {var subQ0=sQuery(id+"F18.wireOp",EDGE,"E40");Q0=makeQuery(id+"F35.boolean.opBoolean","MERGE",FACE,{"derivedFrom":[makeQuery(id+"F19.opExtrude","CAP_FACE",FACE,{"disambiguationData":[OSD([sQuery(id+"F18.wireOp",EDGE,"E39"),subQ0,sQuery(id+"F18.wireOp",EDGE,"E41"),sQuery(id+"F18.wireOp",EDGE,"E42")])],"isStart":false}),makeQuery(id+"F35.opExtrude","CAP_FACE",FACE,{"disambiguationData":[OSD([subQ0,sQuery(id+"F32.wireOp",EDGE,"E74.bottom"),sQuery(id+"F32.wireOp",EDGE,"E74.right"),sQuery(id+"F32.wireOp",EDGE,"E75.bottom"),sQuery(id+"F32.wireOp",EDGE,"E75.right")])],"isStart":false})]});}
            var sketch = newSketch(context, id + "F36", { "sketchPlane" : qUnion([Q0])});
            skCircle(sketch, "E76", {"center": v(0, 0) * mm, "radius": 2.1 * mm});
            skCircle(sketch, "E77.0.1.0", {"center": v(0, 6.35) * mm, "radius": 2.1 * mm});
            skCircle(sketch, "E77.0.2.0", {"center": v(0, 12.7) * mm, "radius": 2.1 * mm});
            skCircle(sketch, "E77.0.3.0", {"center": v(0, 19.05) * mm, "radius": 2.1 * mm});
            skCircle(sketch, "E77.0.4.0", {"center": v(0, 25.4) * mm, "radius": 2.1 * mm});
            skCircle(sketch, "E77.1.0.0", {"center": v(25.4, 0) * mm, "radius": 2.1 * mm});
            skCircle(sketch, "E77.1.1.0", {"center": v(25.4, 6.35) * mm, "radius": 2.1 * mm});
            skCircle(sketch, "E77.1.2.0", {"center": v(25.4, 12.7) * mm, "radius": 2.1 * mm});
            skCircle(sketch, "E77.1.3.0", {"center": v(25.4, 19.05) * mm, "radius": 2.1 * mm});
            skCircle(sketch, "E77.1.4.0", {"center": v(25.4, 25.4) * mm, "radius": 2.1 * mm});
            skCircle(sketch, "E77.2.0.0", {"center": v(50.8, 0) * mm, "radius": 2.1 * mm});
            skCircle(sketch, "E77.2.1.0", {"center": v(50.8, 6.35) * mm, "radius": 2.1 * mm});
            skCircle(sketch, "E77.2.2.0", {"center": v(50.8, 12.7) * mm, "radius": 2.1 * mm});
            skCircle(sketch, "E77.2.3.0", {"center": v(50.8, 19.05) * mm, "radius": 2.1 * mm});
            skCircle(sketch, "E77.2.4.0", {"center": v(50.8, 25.4) * mm, "radius": 2.1 * mm});
            skLineSegment(sketch, "E77.direction1", {"start": v(0, 0) * mm, "end": v(25.4, 0) * mm, "construction": true});
            skLineSegment(sketch, "E77.direction2", {"start": v(0, 0) * mm, "end": v(0, 6.35) * mm, "construction": true});
            skSolve(sketch);
        }
        {
            var Q0;
            Q0=makeQuery(id+"F36.imprint","IMPRINT",FACE,{"disambiguationData":[TD([[makeQuery(id+"F36.imprint","IMPRINT",EDGE,{"derivedFrom":sQuery(id+"F36.wireOp",EDGE,"E76")}),1.0]])]});
            var Q1;
            Q1=makeQuery(id+"F36.imprint","IMPRINT",FACE,{"disambiguationData":[TD([[makeQuery(id+"F36.imprint","IMPRINT",EDGE,{"derivedFrom":sQuery(id+"F36.wireOp",EDGE,"E77.0.1.0")}),1.0]])]});
            var Q2;
            Q2=makeQuery(id+"F36.imprint","IMPRINT",FACE,{"disambiguationData":[TD([[makeQuery(id+"F36.imprint","IMPRINT",EDGE,{"derivedFrom":sQuery(id+"F36.wireOp",EDGE,"E77.0.3.0")}),1.0]])]});
            var Q3;
            Q3=makeQuery(id+"F36.imprint","IMPRINT",FACE,{"disambiguationData":[TD([[makeQuery(id+"F36.imprint","IMPRINT",EDGE,{"derivedFrom":sQuery(id+"F36.wireOp",EDGE,"E77.0.4.0")}),1.0]])]});
            var Q4;
            Q4=makeQuery(id+"F36.imprint","IMPRINT",FACE,{"disambiguationData":[TD([[makeQuery(id+"F36.imprint","IMPRINT",EDGE,{"derivedFrom":sQuery(id+"F36.wireOp",EDGE,"E77.0.2.0")}),1.0]])]});
            extrude(context, id + "F37", {"entities" : qUnion([Q0, Q1, Q2, Q3, Q4]), "operationType" : NewBodyOperationType.REMOVE, "oppositeDirection" : true, "depth" : 25.4 * mm});
        }
        {
            var Q0;
            Q0=makeQuery(id+"F5.opExtrude","SWEPT_FACE",FACE,{"disambiguationData":[OSD([sQuery(id+"F4.wireOp",EDGE,"E11.top")])]});
            extrude(context, id + "F38", {"entities" : qUnion([Q0]), "operationType" : NewBodyOperationType.ADD, "depth" : 8.9 * mm});
        }
        {
            var Q0;
            {var subQ0=sQuery(id+"F2.wireOp",EDGE,"E8");var subQ1=sQuery(id+"F2.wireOp",EDGE,"E7");var subQ2=sQuery(id+"F2.wireOp",EDGE,"E4");var subQ3=sQuery(id+"F6.wireOp",EDGE,"E16");var subQ4=sQuery(id+"F6.wireOp",EDGE,"E13.left");var subQ5=sQuery(id+"F6.wireOp",EDGE,"E13.bottom");var subQ6=sQuery(id+"F2.wireOp",EDGE,"E3");var subQ7=sQuery(id+"F6.wireOp",EDGE,"E15");var subQ8=sQuery(id+"F6.wireOp",EDGE,"E14.left");var subQ9=sQuery(id+"F6.wireOp",EDGE,"E14.bottom");var subQ10=sQuery(id+"F14.wireOp",EDGE,"E34.left");var subQ11=sQuery(id+"F14.wireOp",EDGE,"E34.right");Q0=makeQuery(id+"F19.boolean.opBoolean","SPLIT",FACE,{"disambiguationData":[TD([makeQuery(id+"F1.opExtrude","SWEPT_FACE",FACE,{"disambiguationData":[OSD([sQuery(id+"F0.wireOp",EDGE,"E1")])]}),makeQuery(id+"F1.opExtrude","SWEPT_FACE",FACE,{"disambiguationData":[OSD([sQuery(id+"F0.wireOp",EDGE,"E2.left")])]}),makeQuery(id+"F1.opExtrude","SWEPT_FACE",FACE,{"disambiguationData":[OSD([sQuery(id+"F0.wireOp",EDGE,"E2.right")])]}),makeQuery(id+"F3.opExtrude","SWEPT_FACE",FACE,{"disambiguationData":[OSD([subQ6])]}),makeQuery(id+"F3.opExtrude","SWEPT_FACE",FACE,{"disambiguationData":[OSD([subQ2])]}),makeQuery(id+"F3.opExtrude","SWEPT_FACE",FACE,{"disambiguationData":[OSD([subQ1])]}),makeQuery(id+"F3.opExtrude","SWEPT_FACE",FACE,{"disambiguationData":[OSD([subQ0])]}),makeQuery(id+"F5.opExtrude","SWEPT_FACE",FACE,{"disambiguationData":[OSD([sQuery(id+"F4.wireOp",EDGE,"E10.left"),sQuery(id+"F4.wireOp",EDGE,"E11.left"),sQuery(id+"F4.wireOp",EDGE,"E12.left")])]}),makeQuery(id+"F5.opExtrude","SWEPT_FACE",FACE,{"disambiguationData":[OSD([sQuery(id+"F4.wireOp",EDGE,"E10.right"),sQuery(id+"F4.wireOp",EDGE,"E11.right"),sQuery(id+"F4.wireOp",EDGE,"E12.right")])]}),makeQuery(id+"F7.opExtrude","CAP_FACE",FACE,{"disambiguationData":[OSD([subQ5,subQ4,subQ3])],"isStart":true}),makeQuery(id+"F7.opExtrude","CAP_FACE",FACE,{"disambiguationData":[OSD([subQ5,subQ4,subQ3])],"isStart":false}),makeQuery(id+"F7.opExtrude","CAP_FACE",FACE,{"disambiguationData":[OSD([subQ9,subQ8,subQ7])],"isStart":true}),makeQuery(id+"F7.opExtrude","CAP_FACE",FACE,{"disambiguationData":[OSD([subQ9,subQ8,subQ7])],"isStart":false}),makeQuery(id+"F15.opExtrude","SWEPT_FACE",FACE,{"disambiguationData":[OSD([subQ10])]}),makeQuery(id+"F15.opExtrude","SWEPT_FACE",FACE,{"disambiguationData":[OSD([subQ11])]}),makeQuery(id+"F19.opExtrude","SWEPT_FACE",FACE,{"disambiguationData":[OSD([sQuery(id+"F18.wireOp",EDGE,"E40")])]}),makeQuery(id+"F19.opExtrude","SWEPT_FACE",FACE,{"disambiguationData":[OSD([sQuery(id+"F18.wireOp",EDGE,"E41")])]}),makeQuery(id+"F19.opExtrude","SWEPT_FACE",FACE,{"disambiguationData":[OSD([sQuery(id+"F18.wireOp",EDGE,"E42")])]})])],"derivedFrom":makeQuery(id+"F15.boolean.opBoolean","MERGE",FACE,{"derivedFrom":[makeQuery(id+"F3.boolean.opBoolean","MERGE",FACE,{"derivedFrom":[makeQuery(id+"F3.opExtrude","CAP_FACE",FACE,{"disambiguationData":[OSD([subQ6,sQuery(id+"F2.wireOp",EDGE,"E9")])],"isStart":false}),makeQuery(id+"F3.opExtrude","CAP_FACE",FACE,{"disambiguationData":[OSD([sQuery(id+"F0.wireOp",EDGE,"E0"),subQ2,subQ1,subQ0])],"isStart":false})]}),makeQuery(id+"F9.boolean.opBoolean","COPY",FACE,{"derivedFrom":makeQuery(id+"F9.opExtrude","CAP_FACE",FACE,{"disambiguationData":[OSD([sQuery(id+"F8.wireOp",EDGE,"E17")])],"isStart":true})}),makeQuery(id+"F15.opExtrude","CAP_FACE",FACE,{"disambiguationData":[OSD([sQuery(id+"F14.wireOp",EDGE,"E34.bottom"),sQuery(id+"F14.wireOp",EDGE,"E34.top"),subQ10,subQ11,sQuery(id+"F14.wireOp",EDGE,"E35.top"),sQuery(id+"F14.wireOp",EDGE,"E35.left"),sQuery(id+"F14.wireOp",EDGE,"E35.right"),sQuery(id+"F14.wireOp",EDGE,"E36.trimOffspring")])],"isStart":false})]})});}
            var sketch = newSketch(context, id + "F39", { "sketchPlane" : qUnion([Q0])});
            skCircle(sketch, "E78", {"center": v(0, 0) * mm, "radius": 95.25 * mm});
            skCircle(sketch, "E79", {"center": v(0, 0) * mm, "radius": 82.55 * mm});
            skLineSegment(sketch, "E80", {"start": v(63.5, -71) * mm, "end": v(63.5, -52.75) * mm});
            skLineSegment(sketch, "E81", {"start": v(-63.5, -71) * mm, "end": v(-63.5, -52.75) * mm});
            skSolve(sketch);
        }
        {
            var Q0;
            {var subQ2=sQuery(id+"F39.wireOp",EDGE,"E80");Q0=makeQuery(id+"F39.imprint","IMPRINT",FACE,{"disambiguationData":[TD([[makeQuery(id+"F39.imprint","IMPRINT",EDGE,{"derivedFrom":subQ2}),-1.0]])]});}
            extrude(context, id + "F40", {"entities" : qUnion([Q0]), "operationType" : NewBodyOperationType.ADD, "depth" : 50.8 * mm});
        }
        {
            var Q0;
            {var subQ0=sQuery(id+"F18.wireOp",EDGE,"E40");Q0=makeQuery(id+"F40.boolean.opBoolean","MERGE",FACE,{"derivedFrom":[makeQuery(id+"F35.boolean.opBoolean","MERGE",FACE,{"derivedFrom":[makeQuery(id+"F19.opExtrude","CAP_FACE",FACE,{"disambiguationData":[OSD([sQuery(id+"F18.wireOp",EDGE,"E39"),subQ0,sQuery(id+"F18.wireOp",EDGE,"E41"),sQuery(id+"F18.wireOp",EDGE,"E42")])],"isStart":false}),makeQuery(id+"F35.opExtrude","CAP_FACE",FACE,{"disambiguationData":[OSD([subQ0,sQuery(id+"F32.wireOp",EDGE,"E74.bottom"),sQuery(id+"F32.wireOp",EDGE,"E74.right"),sQuery(id+"F32.wireOp",EDGE,"E75.bottom"),sQuery(id+"F32.wireOp",EDGE,"E75.right")])],"isStart":false})]}),makeQuery(id+"F40.opExtrude","CAP_FACE",FACE,{"disambiguationData":[OSD([sQuery(id+"F39.wireOp",EDGE,"E78"),sQuery(id+"F39.wireOp",EDGE,"E79"),sQuery(id+"F39.wireOp",EDGE,"E80"),sQuery(id+"F39.wireOp",EDGE,"E81")])],"isStart":false})]});}
            var sketch = newSketch(context, id + "F41", { "sketchPlane" : qUnion([Q0])});
            skLineSegment(sketch, "E82.bottom", {"start": v(6.35, -82.3) * mm, "end": v(-38.1, -82.3) * mm});
            skLineSegment(sketch, "E82.top", {"start": v(6.35, -107.7) * mm, "end": v(-38.1, -107.7) * mm});
            skLineSegment(sketch, "E82.left", {"start": v(6.35, -82.3) * mm, "end": v(6.35, -107.7) * mm});
            skLineSegment(sketch, "E82.right", {"start": v(-38.1, -82.3) * mm, "end": v(-38.1, -107.7) * mm});
            skLineSegment(sketch, "E83.bottom", {"start": v(-6.35, -82.3) * mm, "end": v(38.1, -82.3) * mm});
            skLineSegment(sketch, "E83.top", {"start": v(-6.35, -107.7) * mm, "end": v(38.1, -107.7) * mm});
            skLineSegment(sketch, "E83.left", {"start": v(-6.35, -82.3) * mm, "end": v(-6.35, -107.7) * mm});
            skLineSegment(sketch, "E83.right", {"start": v(38.1, -82.3) * mm, "end": v(38.1, -107.7) * mm});
            skSolve(sketch);
        }
        {
            var Q0;
            Q0 = qSketchRegion(id + "F41", true);
            extrude(context, id + "F42", {"entities" : qUnion([Q0]), "operationType" : NewBodyOperationType.ADD, "oppositeDirection" : true, "depth" : 50.8 * mm});
        }
        {
            var Q0;
            Q0=makeQuery(id+"F30.boolean.opBoolean","COPY",FACE,{"derivedFrom":makeQuery(id+"F30.opExtrude","CAP_FACE",FACE,{"disambiguationData":[OSD([sQuery(id+"F29.wireOp",EDGE,"E72.bottom"),sQuery(id+"F29.wireOp",EDGE,"E72.top"),sQuery(id+"F29.wireOp",EDGE,"E72.left"),sQuery(id+"F29.wireOp",EDGE,"E72.right")])],"isStart":true})});
            extrude(context, id + "F43", {"entities" : qUnion([Q0]), "operationType" : NewBodyOperationType.ADD, "depth" : 6.35 * mm});
        }
    });
